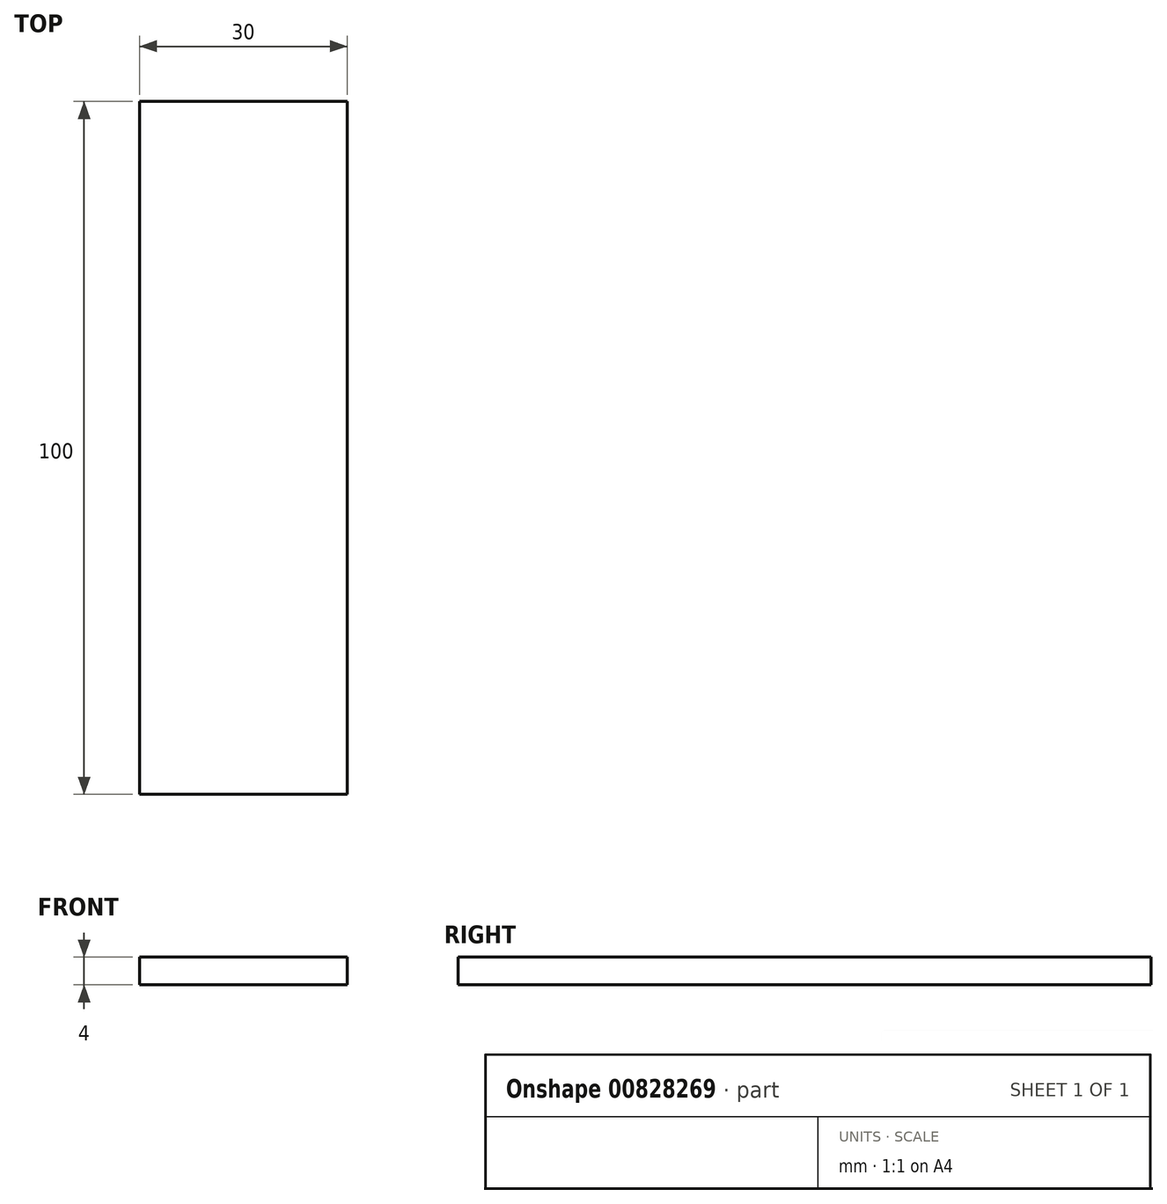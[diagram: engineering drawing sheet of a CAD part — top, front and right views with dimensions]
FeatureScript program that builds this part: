
annotation { "Feature Type Name" : "Feature", "Feature Type Description" : "" }
export const myFeature = defineFeature(function(context is Context, id is Id, definition is map)
    precondition{}
    {
        {
            var Q0;
            Q0=qCreatedBy(makeId("Top.planeOp"),FACE);
            var sketch = newSketch(context, id + "F0", { "sketchPlane" : qUnion([Q0])});
            skLineSegment(sketch, "E0.bottom", {"start": v(15, -50) * mm, "end": v(-15, -50) * mm});
            skLineSegment(sketch, "E0.top", {"start": v(15, 50) * mm, "end": v(-15, 50) * mm});
            skLineSegment(sketch, "E0.left", {"start": v(15, -50) * mm, "end": v(15, 50) * mm});
            skLineSegment(sketch, "E0.right", {"start": v(-15, -50) * mm, "end": v(-15, 50) * mm});
            skPoint(sketch, "E0.middle", {"position": v(0, 0) * mm});
            skSolve(sketch);
        }
        {
            var Q0;
            Q0=makeQuery(id+"F0.imprint","IMPRINT",FACE,{"disambiguationData":[TD([[makeQuery(id+"F0.imprint","IMPRINT",EDGE,{"derivedFrom":sQuery(id+"F0.wireOp",EDGE,"E0.bottom")}),-1.0]])]});
            extrude(context, id + "F1", {"entities" : qUnion([Q0]), "depth" : 4 * mm, "offsetDistance" : 25 * mm});
        }
    });
